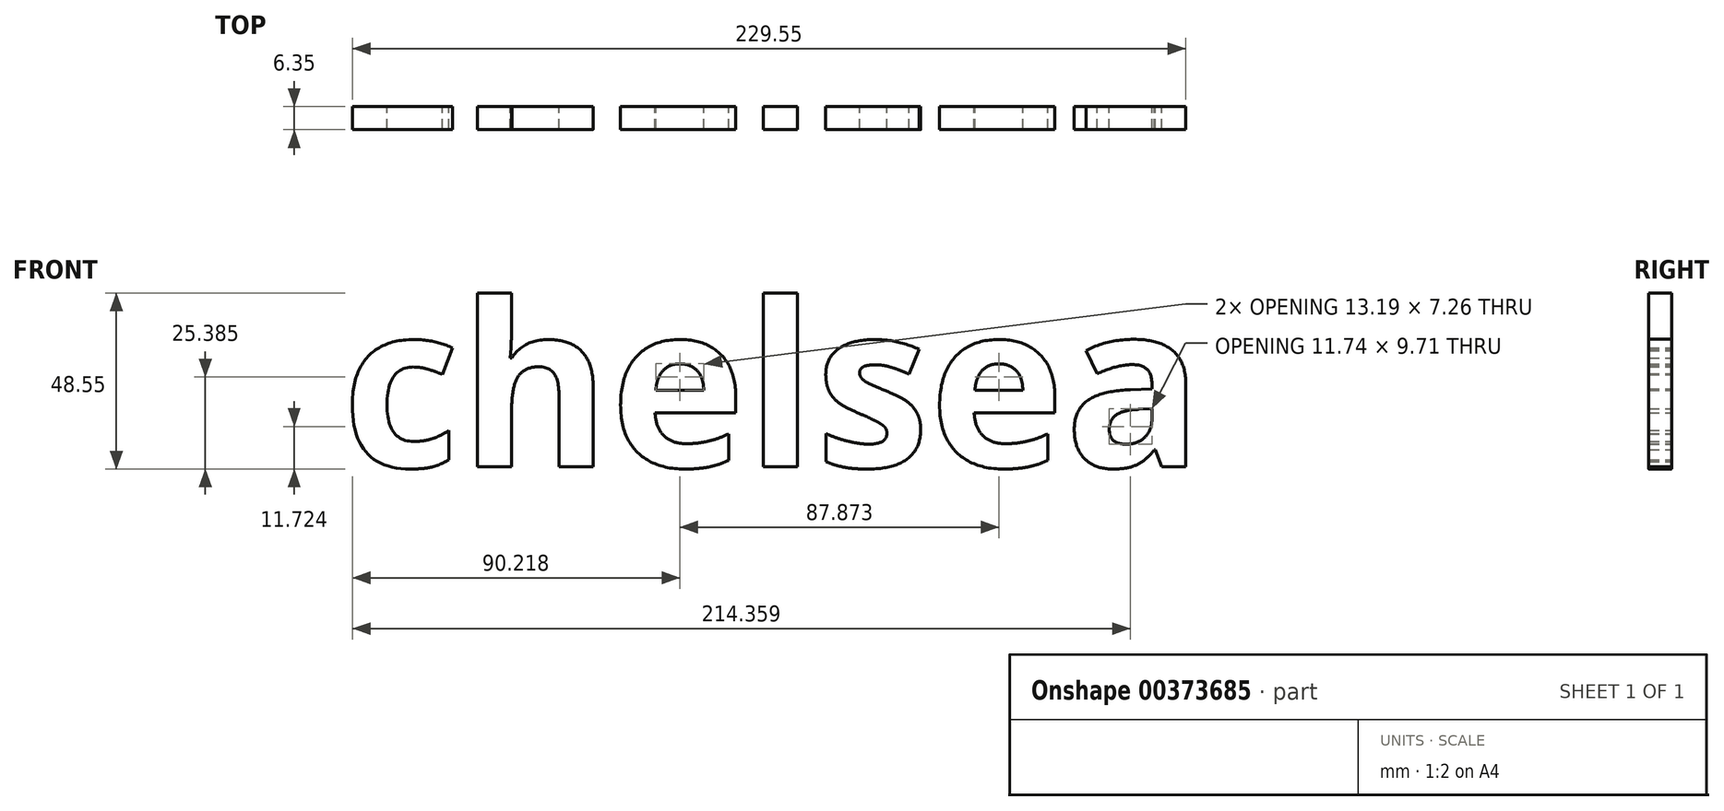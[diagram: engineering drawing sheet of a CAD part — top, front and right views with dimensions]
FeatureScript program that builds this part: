
annotation { "Feature Type Name" : "Feature", "Feature Type Description" : "" }
export const myFeature = defineFeature(function(context is Context, id is Id, definition is map)
    precondition{}
    {
        {
            var Q0;
            Q0=qCreatedBy(makeId("Front.planeOp"),FACE);
            var sketch = newSketch(context, id + "F0", { "sketchPlane" : qUnion([Q0])});
            skText(sketch, "E0", { "text": "chelsea", "fontName": "OpenSans-Bold.ttf"});
            const initialGuessF0  = {"E0": [-0.11674, -0.02057, 1, 0, 0.04542]};
            skSetInitialGuess(sketch, initialGuessF0);
            skSolve(sketch);
        }
        {
            var Q0;
            Q0=makeQuery(id+"F0.imprint","IMPRINT",FACE,{"disambiguationData":[TD([[makeQuery(id+"F0.imprint","IMPRINT",EDGE,{"derivedFrom":sQuery(id+"F0.wireOp",EDGE,"E0.sketch_text.stroke-14")}),-1.0]])]});
            var Q1;
            Q1 = qSketchRegion(id + "F0", true);
            extrude(context, id + "F1", {"entities" : qUnion([Q0, Q1]), "depth" : 6.35 * mm});
        }
    });
